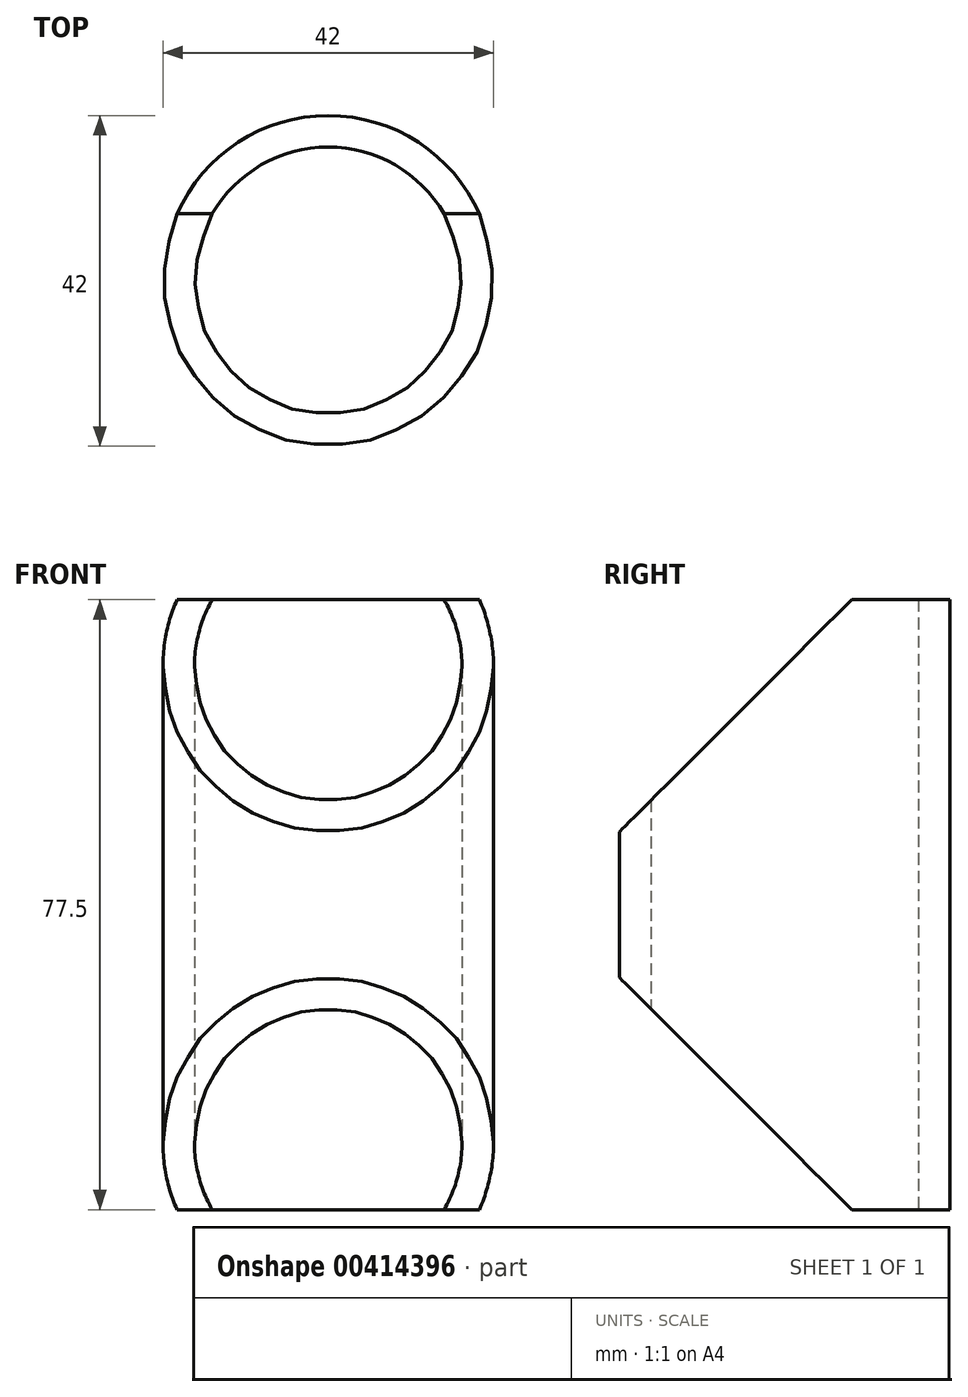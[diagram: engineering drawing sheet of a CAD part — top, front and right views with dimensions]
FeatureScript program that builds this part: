
annotation { "Feature Type Name" : "Feature", "Feature Type Description" : "" }
export const myFeature = defineFeature(function(context is Context, id is Id, definition is map)
    precondition{}
    {
        {
            var Q0;
            Q0=qCreatedBy(makeId("Top.planeOp"),FACE);
            var sketch = newSketch(context, id + "F0", { "sketchPlane" : qUnion([Q0])});
            skCircle(sketch, "E0", {"center": v(0, 0) * mm, "radius": 17 * mm});
            skCircle(sketch, "E1.0", {"center": v(0, 0) * mm, "radius": 21 * mm});
            skSolve(sketch);
        }
        {
            var Q0;
            Q0=qSketchRegion(id+"F0",true);
            extrude(context, id + "F1", {"entities" : qUnion([Q0]), "endBound" : BoundingType.SYMMETRIC, "depth" : 77.5 * mm});
        }
        {
            var Q0;
            Q0=qCreatedBy(makeId("Right.planeOp"),FACE);
            var sketch = newSketch(context, id + "F2", { "sketchPlane" : qUnion([Q0])});
            skLineSegment(sketch, "E2", {"start": v(8.5, 38.75) * mm, "end": v(-21, 9.25) * mm});
            skLineSegment(sketch, "E3", {"start": v(8.5, 38.75) * mm, "end": v(21, 38.75) * mm});
            skLineSegment(sketch, "E4", {"start": v(-21, 9.25) * mm, "end": v(-21, 48.75) * mm});
            skLineSegment(sketch, "E5", {"start": v(-21, 48.75) * mm, "end": v(21, 48.75) * mm});
            skLineSegment(sketch, "E6", {"start": v(21, 48.75) * mm, "end": v(21, 38.75) * mm});
            skPoint(sketch, "E7", {"position": v(0, 48.75) * mm});
            skLineSegment(sketch, "E8.MirrorCS", {"start": v(8.5, -38.75) * mm, "end": v(21, -38.75) * mm});
            skLineSegment(sketch, "E9.MirrorCS", {"start": v(-21, -48.75) * mm, "end": v(21, -48.75) * mm});
            skLineSegment(sketch, "E10.MirrorCS", {"start": v(8.5, -38.75) * mm, "end": v(-21, -9.25) * mm});
            skLineSegment(sketch, "E11.MirrorCS", {"start": v(21, -48.75) * mm, "end": v(21, -38.75) * mm});
            skLineSegment(sketch, "E12.MirrorCS", {"start": v(-21, -9.25) * mm, "end": v(-21, -48.75) * mm});
            skPoint(sketch, "E13.MirrorP", {"position": v(0, -48.75) * mm});
            skSolve(sketch);
        }
        {
            var Q0;
            Q0=qSketchRegion(id+"F2",true);
            extrude(context, id + "F3", {"entities" : qUnion([Q0]), "operationType" : NewBodyOperationType.REMOVE, "endBound" : BoundingType.SYMMETRIC, "oppositeDirection" : true, "depth" : 42 * mm});
        }
    });
